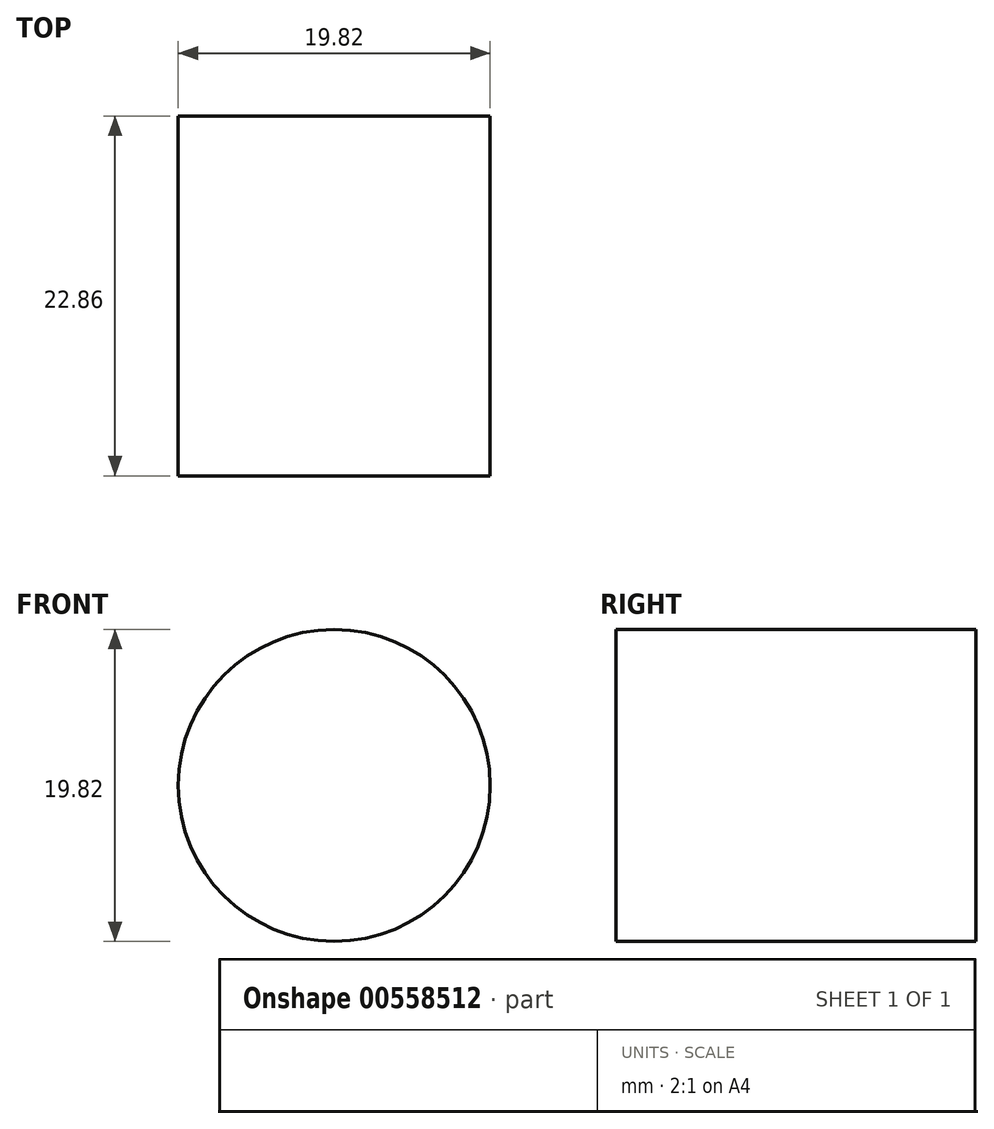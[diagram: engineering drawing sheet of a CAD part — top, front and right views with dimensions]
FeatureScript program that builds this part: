
annotation { "Feature Type Name" : "Feature", "Feature Type Description" : "" }
export const myFeature = defineFeature(function(context is Context, id is Id, definition is map)
    precondition{}
    {
        {
            var Q0;
            Q0=qCreatedBy(makeId("Front.planeOp"),FACE);
            var sketch = newSketch(context, id + "F0", { "sketchPlane" : qUnion([Q0])});
            skCircle(sketch, "E0", {"center": v(0, 0) * mm, "radius": 9.9 * mm});
            skSolve(sketch);
        }
        {
            var Q0;
            Q0=makeQuery(id+"F0.imprint","IMPRINT",FACE,{"disambiguationData":[TD([[makeQuery(id+"F0.imprint","IMPRINT",EDGE,{"derivedFrom":sQuery(id+"F0.wireOp",EDGE,"E0")}),1.0]])]});
            extrude(context, id + "F1", {"entities" : qUnion([Q0]), "depth" : 22.86 * mm, "offsetDistance" : 25.4 * mm});
        }
    });
